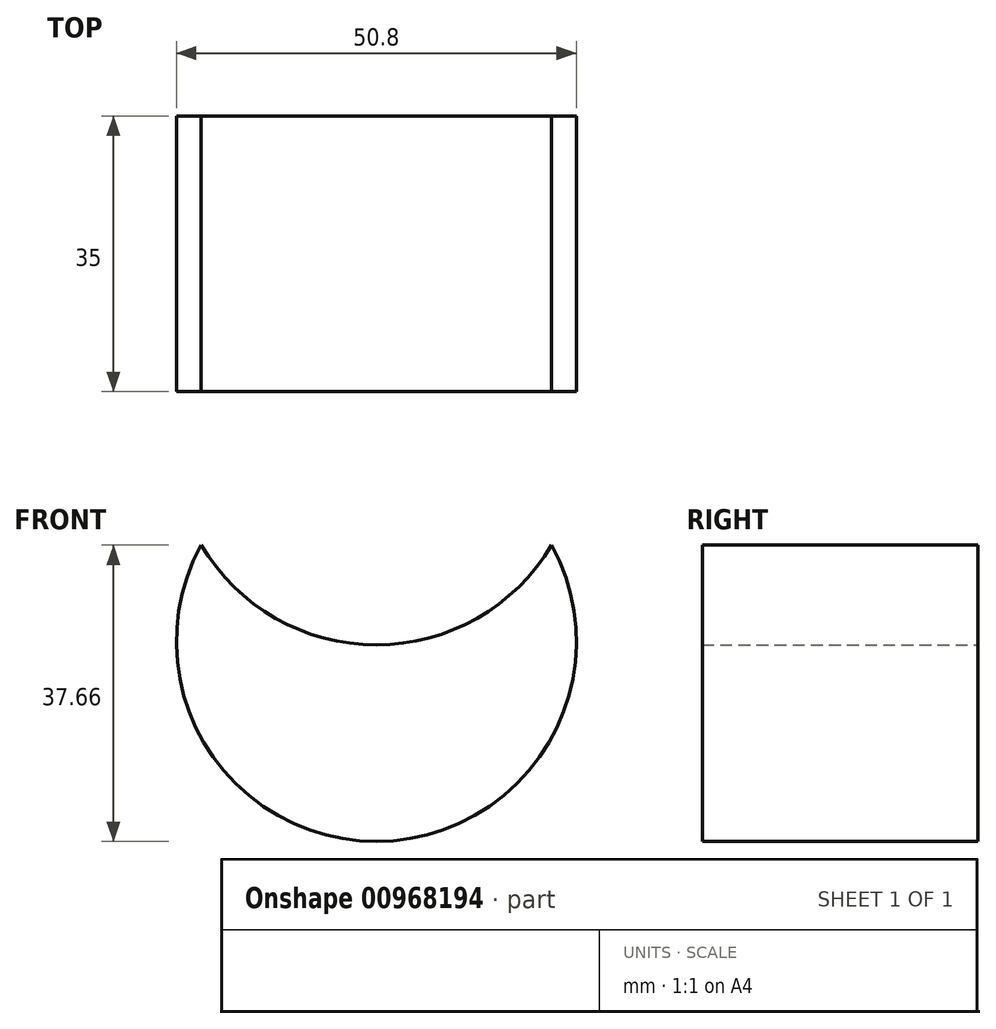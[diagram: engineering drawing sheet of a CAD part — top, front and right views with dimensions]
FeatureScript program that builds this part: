
annotation { "Feature Type Name" : "Feature", "Feature Type Description" : "" }
export const myFeature = defineFeature(function(context is Context, id is Id, definition is map)
    precondition{}
    {
        {
            var Q0;
            Q0=qCreatedBy(makeId("Front.planeOp"),FACE);
            var sketch = newSketch(context, id + "F0", { "sketchPlane" : qUnion([Q0])});
            skArc(sketch, "E0", {"start": v(-22.24, 12.26) * mm, "mid": v(0, -25.4) * mm, "end": v(22.24, 12.26) * mm});
            skArc(sketch, "E1", {"start": v(-22.24, 12.26) * mm, "mid": v(0, -0.43) * mm, "end": v(22.24, 12.26) * mm});
            skSolve(sketch);
        }
        {
            var Q0;
            Q0 = qSketchRegion(id + "F0", true);
            extrude(context, id + "F1", {"entities" : qUnion([Q0]), "depth" : 35 * mm, "offsetDistance" : 25 * mm});
        }
    });
